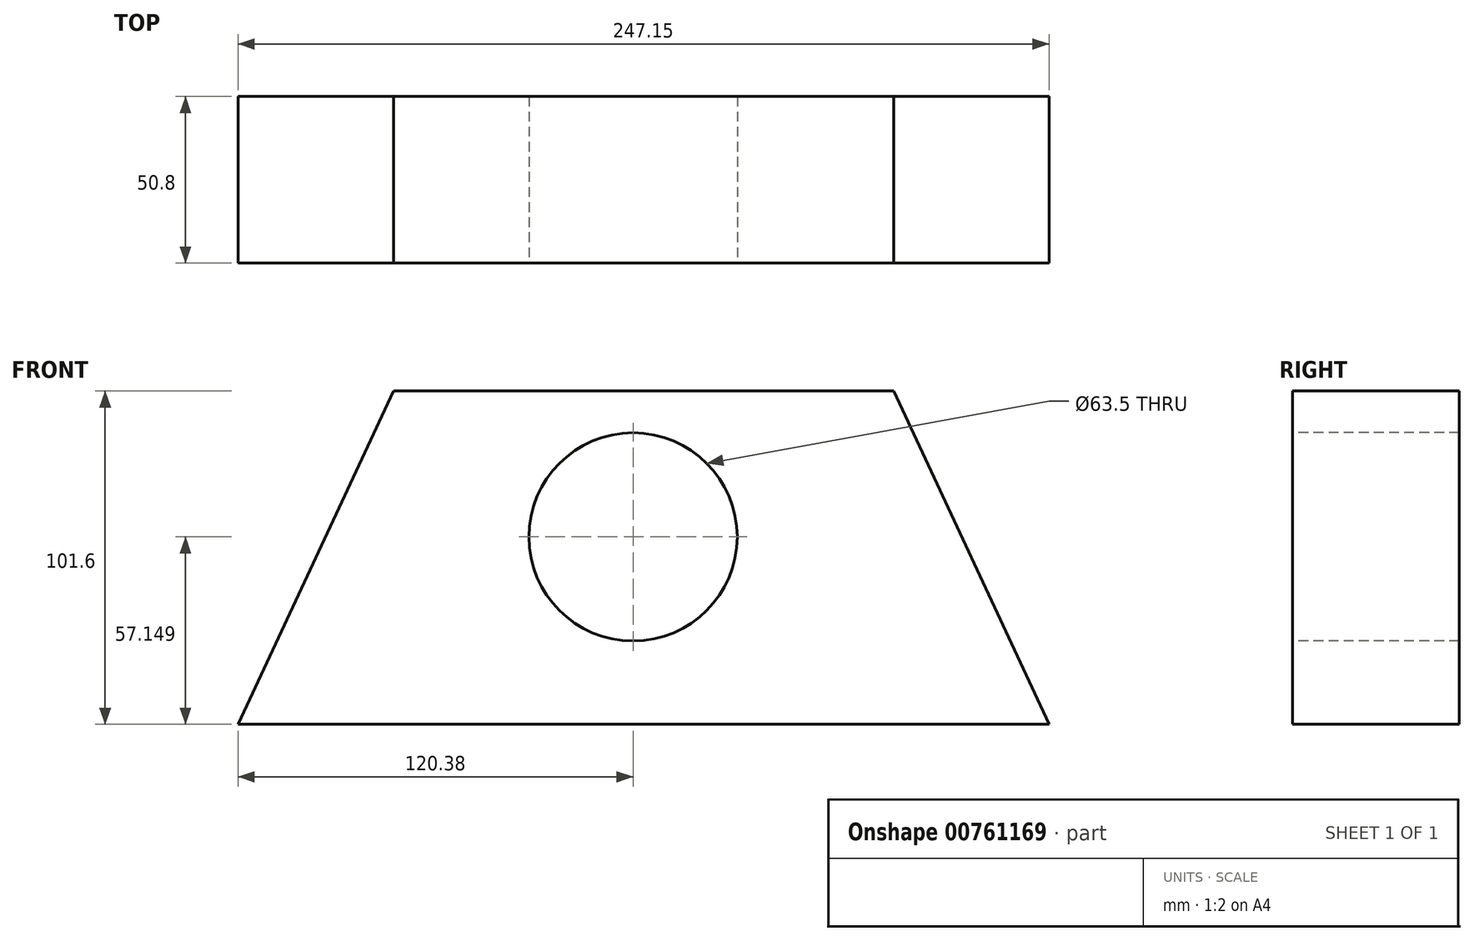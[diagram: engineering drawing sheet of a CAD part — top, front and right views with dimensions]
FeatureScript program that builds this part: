
annotation { "Feature Type Name" : "Feature", "Feature Type Description" : "" }
export const myFeature = defineFeature(function(context is Context, id is Id, definition is map)
    precondition{}
    {
        {
            var Q0;
            Q0=qCreatedBy(makeId("Front.planeOp"),FACE);
            var sketch = newSketch(context, id + "F0", { "sketchPlane" : qUnion([Q0])});
            skLineSegment(sketch, "E0.bottom", {"start": v(-73, 91.29) * mm, "end": v(79.4, 91.29) * mm});
            skLineSegment(sketch, "E0.top", {"start": v(-120.38, -10.31) * mm, "end": v(126.77, -10.31) * mm});
            skLineSegment(sketch, "E1", {"start": v(-120.38, -10.31) * mm, "end": v(-73, 91.29) * mm});
            skLineSegment(sketch, "E2", {"start": v(126.77, -10.31) * mm, "end": v(79.4, 91.29) * mm});
            skSolve(sketch);
        }
        {
            var Q0;
            Q0=makeQuery(id+"F0.imprint","IMPRINT",FACE,{"disambiguationData":[TD([[makeQuery(id+"F0.imprint","IMPRINT",EDGE,{"derivedFrom":sQuery(id+"F0.wireOp",EDGE,"E0.bottom")}),-1.0]])]});
            extrude(context, id + "F1", {"entities" : qUnion([Q0]), "depth" : 50.8 * mm, "offsetDistance" : 25.4 * mm});
        }
        {
            var Q0;
            Q0=makeQuery(id+"F1.opExtrude","CAP_FACE",FACE,{"disambiguationData":[OSD([sQuery(id+"F0.wireOp",EDGE,"E0.bottom"),sQuery(id+"F0.wireOp",EDGE,"E0.top"),sQuery(id+"F0.wireOp",EDGE,"E1"),sQuery(id+"F0.wireOp",EDGE,"E2")])],"isStart":false});
            var sketch = newSketch(context, id + "F2", { "sketchPlane" : qUnion([Q0])});
            skCircle(sketch, "E3", {"center": v(0, 46.84) * mm, "radius": 31.75 * mm});
            skSolve(sketch);
        }
        {
            var Q0;
            Q0=makeQuery(id+"F2.imprint","IMPRINT",FACE,{"disambiguationData":[TD([[makeQuery(id+"F2.imprint","IMPRINT",EDGE,{"derivedFrom":sQuery(id+"F2.wireOp",EDGE,"E3")}),1.0]])]});
            extrude(context, id + "F3", {"entities" : qUnion([Q0]), "operationType" : NewBodyOperationType.REMOVE, "oppositeDirection" : true, "depth" : 50.8 * mm, "offsetDistance" : 25.4 * mm});
        }
    });
